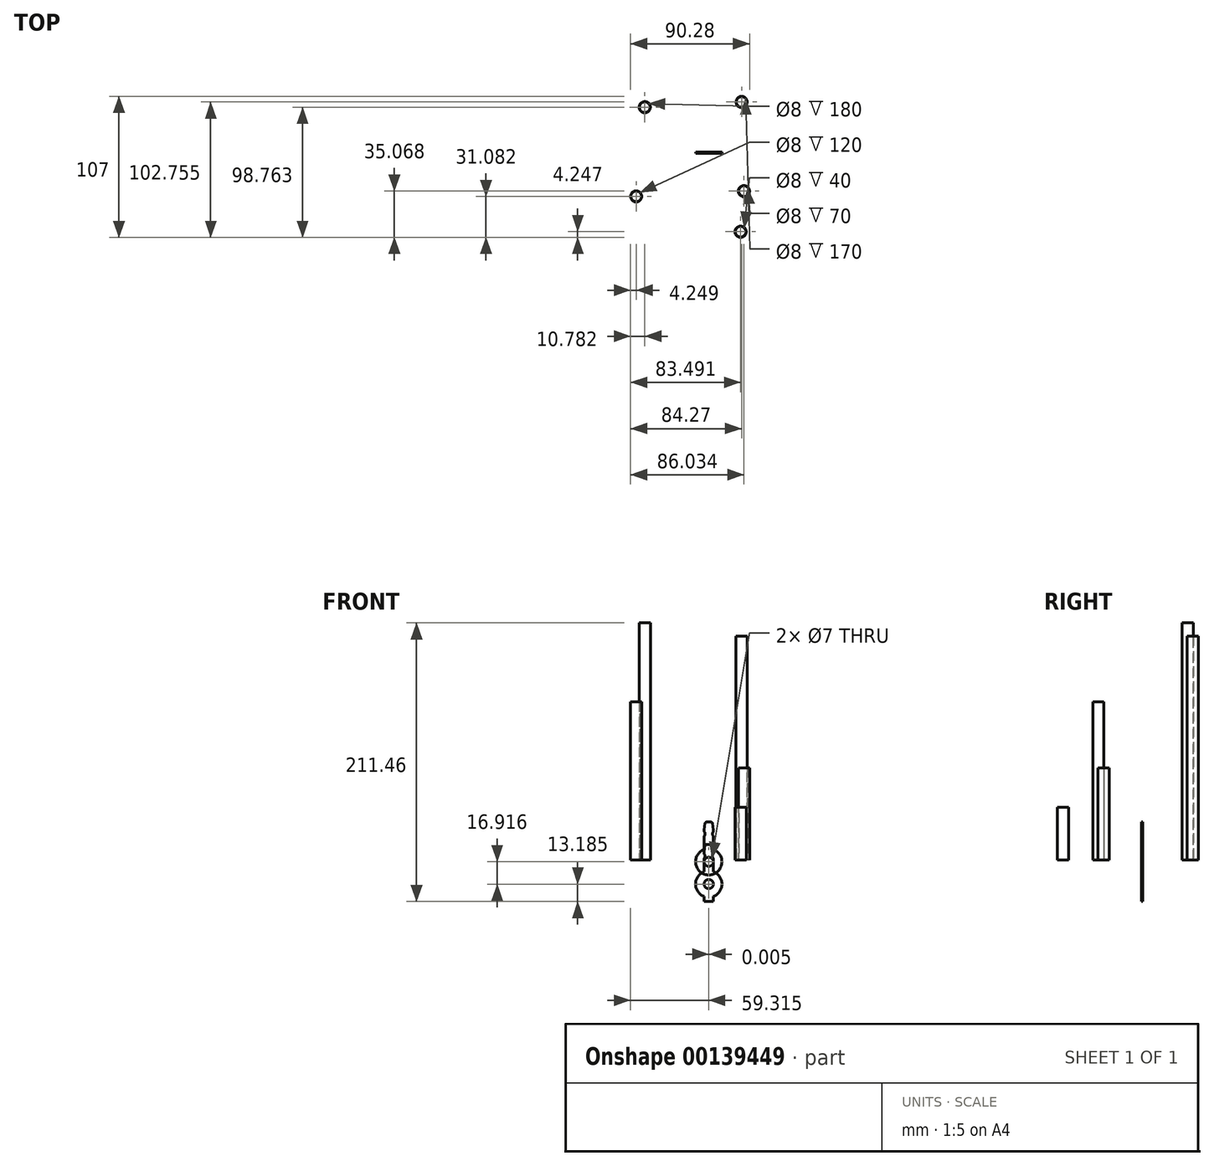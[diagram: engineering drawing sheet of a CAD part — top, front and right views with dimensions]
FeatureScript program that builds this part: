
annotation { "Feature Type Name" : "Feature", "Feature Type Description" : "" }
export const myFeature = defineFeature(function(context is Context, id is Id, definition is map)
    precondition{}
    {
        {
            var Q0;
            Q0=qCreatedBy(makeId("Front.planeOp"),FACE);
            var sketch = newSketch(context, id + "F0", { "sketchPlane" : qUnion([Q0])});
            skLineSegment(sketch, "E0", {"start": v(-2.76, 28) * mm, "end": v(-3.58, 22.9) * mm});
            skLineSegment(sketch, "E1", {"start": v(-3.58, 22.9) * mm, "end": v(-3.58, 21.67) * mm});
            skLineSegment(sketch, "E2", {"start": v(-3.6, 17.97) * mm, "end": v(-3.6, 11.83) * mm});
            skLineSegment(sketch, "E3", {"start": v(-3.6, 11.83) * mm, "end": v(3.6, 11.83) * mm});
            skLineSegment(sketch, "E4", {"start": v(3.6, 11.83) * mm, "end": v(3.6, 17.97) * mm});
            skLineSegment(sketch, "E5", {"start": v(3.6, 21.64) * mm, "end": v(3.6, 22.9) * mm});
            skLineSegment(sketch, "E6", {"start": v(3.6, 22.9) * mm, "end": v(2.73, 27.97) * mm});
            skLineSegment(sketch, "E7", {"start": v(1.76, 28.8) * mm, "end": v(-1.7, 28.8) * mm});
            skArc(sketch, "E8", {"start": v(-1.7, 28.8) * mm, "mid": v(-2.36, 28.58) * mm, "end": v(-2.76, 28) * mm});
            skArc(sketch, "E9", {"start": v(2.73, 27.97) * mm, "mid": v(2.4, 28.57) * mm, "end": v(1.76, 28.8) * mm});
            skArc(sketch, "E10", {"start": v(-3.6, 17.97) * mm, "mid": v(-2.8, 19.81) * mm, "end": v(-3.58, 21.67) * mm});
            skArc(sketch, "E11", {"start": v(3.6, 21.64) * mm, "mid": v(2.8, 19.8) * mm, "end": v(3.6, 17.97) * mm});
            skLineSegment(sketch, "E12", {"start": v(-3.6, 11.83) * mm, "end": v(-3.6, 7.97) * mm});
            skLineSegment(sketch, "E13", {"start": v(-3.6, 7.97) * mm, "end": v(3.6, 7.97) * mm});
            skLineSegment(sketch, "E14", {"start": v(3.6, 7.97) * mm, "end": v(3.6, 11.83) * mm});
            skCircle(sketch, "E15", {"center": v(0, -1.36) * mm, "radius": 10 * mm});
            skCircle(sketch, "E16", {"center": v(0, -1.36) * mm, "radius": 3.5 * mm});
            skSolve(sketch);
        }
        {
            var Q0;
            Q0=makeQuery(id+"F0.imprint","IMPRINT",FACE,{"disambiguationData":[TD([[makeQuery(id+"F0.imprint","IMPRINT",EDGE,{"derivedFrom":sQuery(id+"F0.wireOp",EDGE,"E0")}),1.0]])]});
            var Q1;
            Q1=makeQuery(id+"F0.imprint","IMPRINT",FACE,{"disambiguationData":[TD([[makeQuery(id+"F0.imprint","IMPRINT",EDGE,{"derivedFrom":sQuery(id+"F0.wireOp",EDGE,"E3")}),-1.0]])]});
            var Q2;
            {var subQ0=sQuery(id+"F0.wireOp",EDGE,"E13");Q2=makeQuery(id+"F0.imprint","IMPRINT",FACE,{"disambiguationData":[TD([[makeQuery(id+"F0.imprint","IMPRINT",EDGE,{"derivedFrom":subQ0}),1.0]])]});}
            var Q3;
            {var subQ0=sQuery(id+"F0.wireOp",EDGE,"E13");Q3=makeQuery(id+"F0.imprint","IMPRINT",FACE,{"disambiguationData":[TD([[makeQuery(id+"F0.imprint","IMPRINT",EDGE,{"derivedFrom":subQ0}),-1.0]])]});}
            extrude(context, id + "F1", {"entities" : qUnion([Q0, Q1, Q2, Q3]), "depth" : 1 * mm});
        }
        {
            var Q0;
            Q0=qCreatedBy(makeId("Top.planeOp"),FACE);
            var sketch = newSketch(context, id + "F2", { "sketchPlane" : qUnion([Q0])});
            skCircle(sketch, "E17", {"center": v(-55.07, -33.57) * mm, "radius": 4.25 * mm});
            skCircle(sketch, "E18", {"center": v(-55.07, -33.57) * mm, "radius": 4 * mm});
            skSolve(sketch);
        }
        {
            var Q0;
            Q0=makeQuery(id+"F2.imprint","IMPRINT",FACE,{"disambiguationData":[TD([[makeQuery(id+"F2.imprint","IMPRINT",EDGE,{"derivedFrom":sQuery(id+"F2.wireOp",EDGE,"E17")}),1.0]])]});
            extrude(context, id + "F3", {"entities" : qUnion([Q0]), "depth" : 120 * mm});
        }
        {
            var Q0;
            Q0=qCreatedBy(makeId("Top.planeOp"),FACE);
            var sketch = newSketch(context, id + "F4", { "sketchPlane" : qUnion([Q0])});
            skCircle(sketch, "E19", {"center": v(-48.54, 34.11) * mm, "radius": 4.25 * mm});
            skCircle(sketch, "E20", {"center": v(-48.54, 34.11) * mm, "radius": 4 * mm});
            skSolve(sketch);
        }
        {
            var Q0;
            Q0=makeQuery(id+"F4.imprint","IMPRINT",FACE,{"disambiguationData":[TD([[makeQuery(id+"F4.imprint","IMPRINT",EDGE,{"derivedFrom":sQuery(id+"F4.wireOp",EDGE,"E19")}),1.0]])]});
            extrude(context, id + "F5", {"entities" : qUnion([Q0]), "depth" : 180 * mm});
        }
        {
            var Q0;
            Q0=qCreatedBy(makeId("Top.planeOp"),FACE);
            var sketch = newSketch(context, id + "F6", { "sketchPlane" : qUnion([Q0])});
            skCircle(sketch, "E21", {"center": v(24.95, 38.1) * mm, "radius": 4.25 * mm});
            skCircle(sketch, "E22", {"center": v(24.95, 38.1) * mm, "radius": 4 * mm});
            skSolve(sketch);
        }
        {
            var Q0;
            Q0=makeQuery(id+"F6.imprint","IMPRINT",FACE,{"disambiguationData":[TD([[makeQuery(id+"F6.imprint","IMPRINT",EDGE,{"derivedFrom":sQuery(id+"F6.wireOp",EDGE,"E21")}),1.0]])]});
            extrude(context, id + "F7", {"entities" : qUnion([Q0]), "depth" : 170 * mm});
        }
        {
            var Q0;
            Q0=qCreatedBy(makeId("Top.planeOp"),FACE);
            var sketch = newSketch(context, id + "F8", { "sketchPlane" : qUnion([Q0])});
            skCircle(sketch, "E23", {"center": v(26.71, -29.58) * mm, "radius": 4.25 * mm});
            skCircle(sketch, "E24", {"center": v(26.71, -29.58) * mm, "radius": 4 * mm});
            skSolve(sketch);
        }
        {
            var Q0;
            Q0=makeQuery(id+"F8.imprint","IMPRINT",FACE,{"disambiguationData":[TD([[makeQuery(id+"F8.imprint","IMPRINT",EDGE,{"derivedFrom":sQuery(id+"F8.wireOp",EDGE,"E23")}),1.0]])]});
            extrude(context, id + "F9", {"entities" : qUnion([Q0]), "depth" : 70 * mm});
        }
        {
            var Q0;
            Q0=qCreatedBy(makeId("Top.planeOp"),FACE);
            var sketch = newSketch(context, id + "F10", { "sketchPlane" : qUnion([Q0])});
            skCircle(sketch, "E25", {"center": v(24.17, -60.4) * mm, "radius": 4.25 * mm});
            skCircle(sketch, "E26", {"center": v(24.17, -60.4) * mm, "radius": 4 * mm});
            skSolve(sketch);
        }
        {
            var Q0;
            Q0=makeQuery(id+"F10.imprint","IMPRINT",FACE,{"disambiguationData":[TD([[makeQuery(id+"F10.imprint","IMPRINT",EDGE,{"derivedFrom":sQuery(id+"F10.wireOp",EDGE,"E25")}),1.0]])]});
            extrude(context, id + "F11", {"entities" : qUnion([Q0]), "depth" : 40 * mm});
        }
        {
            var Q0;
            Q0=qCreatedBy(makeId("Front.planeOp"),FACE);
            var sketch = newSketch(context, id + "F12", { "sketchPlane" : qUnion([Q0])});
            skLineSegment(sketch, "E27", {"start": v(-2.76, 11.09) * mm, "end": v(-3.59, 5.99) * mm});
            skLineSegment(sketch, "E28", {"start": v(-3.59, 5.99) * mm, "end": v(-3.59, 4.75) * mm});
            skLineSegment(sketch, "E29", {"start": v(-3.6, 1.05) * mm, "end": v(-3.6, -5.09) * mm});
            skLineSegment(sketch, "E30", {"start": v(-3.6, -5.09) * mm, "end": v(3.6, -5.09) * mm});
            skLineSegment(sketch, "E31", {"start": v(3.6, -5.09) * mm, "end": v(3.6, 1.05) * mm});
            skLineSegment(sketch, "E32", {"start": v(3.6, 4.72) * mm, "end": v(3.6, 5.99) * mm});
            skLineSegment(sketch, "E33", {"start": v(3.6, 5.99) * mm, "end": v(2.72, 11.05) * mm});
            skLineSegment(sketch, "E34", {"start": v(1.75, 11.9) * mm, "end": v(-1.7, 11.9) * mm});
            skArc(sketch, "E35", {"start": v(-1.7, 11.9) * mm, "mid": v(-2.36, 11.67) * mm, "end": v(-2.76, 11.09) * mm});
            skArc(sketch, "E36", {"start": v(2.72, 11.05) * mm, "mid": v(2.4, 11.65) * mm, "end": v(1.75, 11.9) * mm});
            skArc(sketch, "E37", {"start": v(-3.6, 1.05) * mm, "mid": v(-2.8, 2.9) * mm, "end": v(-3.59, 4.75) * mm});
            skArc(sketch, "E38", {"start": v(3.6, 4.72) * mm, "mid": v(2.8, 2.89) * mm, "end": v(3.6, 1.05) * mm});
            skLineSegment(sketch, "E39", {"start": v(-3.6, -5.09) * mm, "end": v(-3.6, -8.95) * mm});
            skLineSegment(sketch, "E40", {"start": v(-3.6, -8.95) * mm, "end": v(3.6, -8.95) * mm});
            skLineSegment(sketch, "E41", {"start": v(3.6, -8.95) * mm, "end": v(3.6, -5.09) * mm});
            skCircle(sketch, "E42", {"center": v(0, -18.28) * mm, "radius": 10 * mm});
            skCircle(sketch, "E43", {"center": v(0, -18.28) * mm, "radius": 3.5 * mm});
            skLineSegment(sketch, "E44", {"start": v(0, -18.28) * mm, "end": v(17.8, -18.28) * mm, "construction": true});
            skArc(sketch, "E45.MirrorCS", {"start": v(2.72, -47.6) * mm, "mid": v(2.4, -48.2) * mm, "end": v(1.75, -48.44) * mm});
            skArc(sketch, "E46.MirrorCS", {"start": v(-1.7, -48.44) * mm, "mid": v(-2.36, -48.22) * mm, "end": v(-2.76, -47.64) * mm});
            skLineSegment(sketch, "E47.MirrorCS", {"start": v(3.6, -41.27) * mm, "end": v(3.6, -42.54) * mm});
            skLineSegment(sketch, "E48.MirrorCS", {"start": v(-3.59, -42.54) * mm, "end": v(-3.59, -41.3) * mm});
            skLineSegment(sketch, "E49.MirrorCS", {"start": v(-3.6, -31.46) * mm, "end": v(-3.6, -27.6) * mm});
            skArc(sketch, "E50.MirrorCS", {"start": v(3.6, -41.27) * mm, "mid": v(2.8, -39.44) * mm, "end": v(3.6, -37.6) * mm});
            skArc(sketch, "E51.MirrorCS", {"start": v(-3.6, -37.6) * mm, "mid": v(-2.8, -39.45) * mm, "end": v(-3.59, -41.3) * mm});
            skLineSegment(sketch, "E52.MirrorCS", {"start": v(1.75, -48.44) * mm, "end": v(-1.7, -48.44) * mm});
            skLineSegment(sketch, "E53.MirrorCS", {"start": v(3.6, -42.54) * mm, "end": v(2.72, -47.6) * mm});
            skLineSegment(sketch, "E54.MirrorCS", {"start": v(3.6, -31.46) * mm, "end": v(3.6, -37.6) * mm});
            skLineSegment(sketch, "E55.MirrorCS", {"start": v(-3.6, -31.46) * mm, "end": v(3.6, -31.46) * mm});
            skLineSegment(sketch, "E56.MirrorCS", {"start": v(-3.6, -37.6) * mm, "end": v(-3.6, -31.46) * mm});
            skLineSegment(sketch, "E57.MirrorCS", {"start": v(-2.76, -47.64) * mm, "end": v(-3.59, -42.54) * mm});
            skLineSegment(sketch, "E58.MirrorCS", {"start": v(3.6, -27.6) * mm, "end": v(3.6, -31.46) * mm});
            skLineSegment(sketch, "E59.MirrorCS", {"start": v(-3.6, -27.6) * mm, "end": v(3.6, -27.6) * mm});
            skSolve(sketch);
        }
        {
            var Q0;
            Q0=makeQuery(id+"F12.imprint","IMPRINT",FACE,{"disambiguationData":[TD([[makeQuery(id+"F12.imprint","IMPRINT",EDGE,{"derivedFrom":sQuery(id+"F12.wireOp",EDGE,"E27")}),1.0]])]});
            var Q1;
            Q1=makeQuery(id+"F12.imprint","IMPRINT",FACE,{"disambiguationData":[TD([[makeQuery(id+"F12.imprint","IMPRINT",EDGE,{"derivedFrom":sQuery(id+"F12.wireOp",EDGE,"E30")}),-1.0]])]});
            var Q2;
            {var subQ1=sQuery(id+"F12.wireOp",EDGE,"E40");Q2=makeQuery(id+"F12.imprint","IMPRINT",FACE,{"disambiguationData":[TD([[makeQuery(id+"F12.imprint","IMPRINT",EDGE,{"derivedFrom":subQ1}),-1.0]])]});}
            var Q3;
            {var subQ1=sQuery(id+"F12.wireOp",EDGE,"E49.MirrorCS");Q3=makeQuery(id+"F12.imprint","IMPRINT",FACE,{"disambiguationData":[TD([[makeQuery(id+"F12.imprint","IMPRINT",EDGE,{"derivedFrom":subQ1}),-1.0]])]});}
            var Q4;
            Q4=makeQuery(id+"F12.imprint","IMPRINT",FACE,{"disambiguationData":[TD([[makeQuery(id+"F12.imprint","IMPRINT",EDGE,{"derivedFrom":sQuery(id+"F12.wireOp",EDGE,"E45.MirrorCS")}),-1.0]])]});
            var Q5;
            {var subQ0=sQuery(id+"F12.wireOp",EDGE,"E40");Q5=makeQuery(id+"F12.imprint","IMPRINT",FACE,{"disambiguationData":[TD([[makeQuery(id+"F12.imprint","IMPRINT",EDGE,{"derivedFrom":subQ0}),1.0]])]});}
            var Q6;
            {var subQ0=sQuery(id+"F12.wireOp",EDGE,"E59.MirrorCS");Q6=makeQuery(id+"F12.imprint","IMPRINT",FACE,{"disambiguationData":[TD([[makeQuery(id+"F12.imprint","IMPRINT",EDGE,{"derivedFrom":subQ0}),-1.0]])]});}
            extrude(context, id + "F13", {"entities" : qUnion([Q0, Q1, Q2, Q3, Q4, Q5, Q6]), "depth" : 1 * mm});
        }
    });
